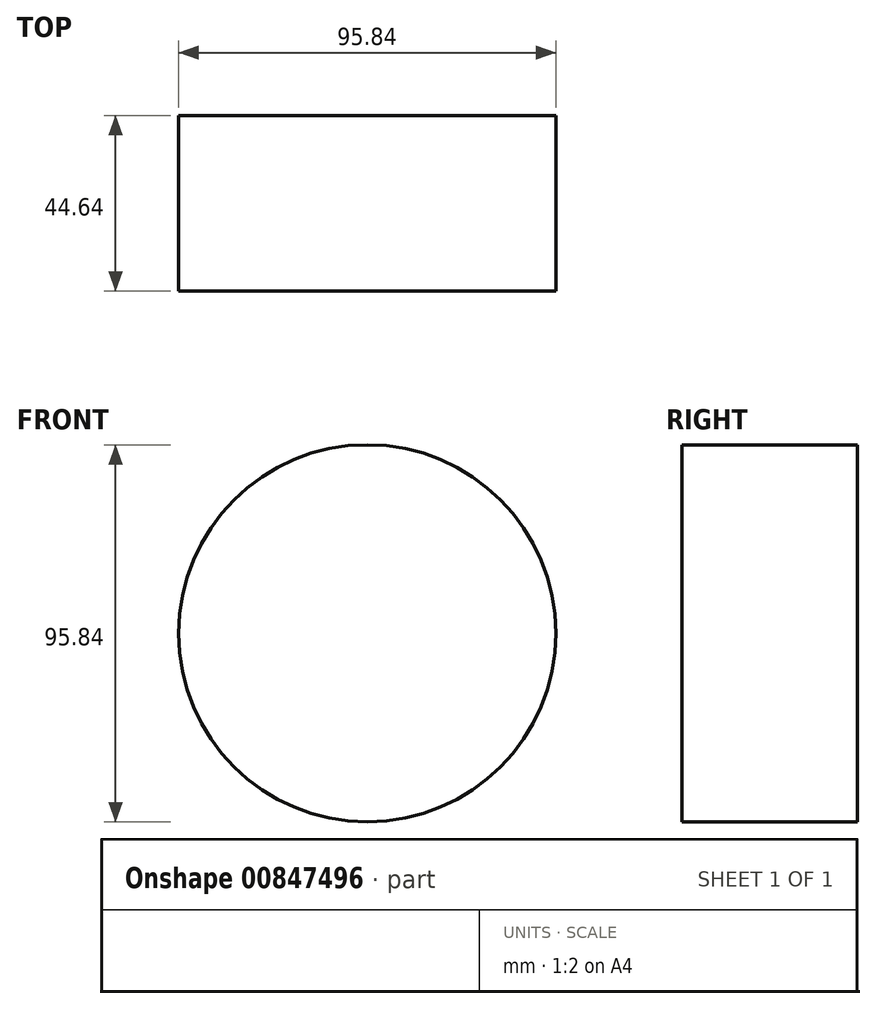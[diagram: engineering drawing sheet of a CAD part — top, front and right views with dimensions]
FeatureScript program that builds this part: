
annotation { "Feature Type Name" : "Feature", "Feature Type Description" : "" }
export const myFeature = defineFeature(function(context is Context, id is Id, definition is map)
    precondition{}
    {
        {
            var Q0;
            Q0=qCreatedBy(makeId("Front.planeOp"),FACE);
            var sketch = newSketch(context, id + "F0", { "sketchPlane" : qUnion([Q0])});
            skCircle(sketch, "E0", {"center": v(0, 0) * mm, "radius": 47.92 * mm});
            skSolve(sketch);
        }
        {
            var Q0;
            Q0=makeQuery(id+"F0.imprint","IMPRINT",FACE,{"disambiguationData":[TD([[makeQuery(id+"F0.imprint","IMPRINT",EDGE,{"derivedFrom":sQuery(id+"F0.wireOp",EDGE,"E0")}),1.0]])]});
            var Q1;
            Q1=sQuery(id+"F0.wireOp",EDGE,"E0");
            extrude(context, id + "F1", {"entities" : qUnion([Q0]), "surfaceEntities" : qUnion([Q1]), "depth" : 44.64 * mm, "offsetDistance" : 25.4 * mm});
        }
    });
